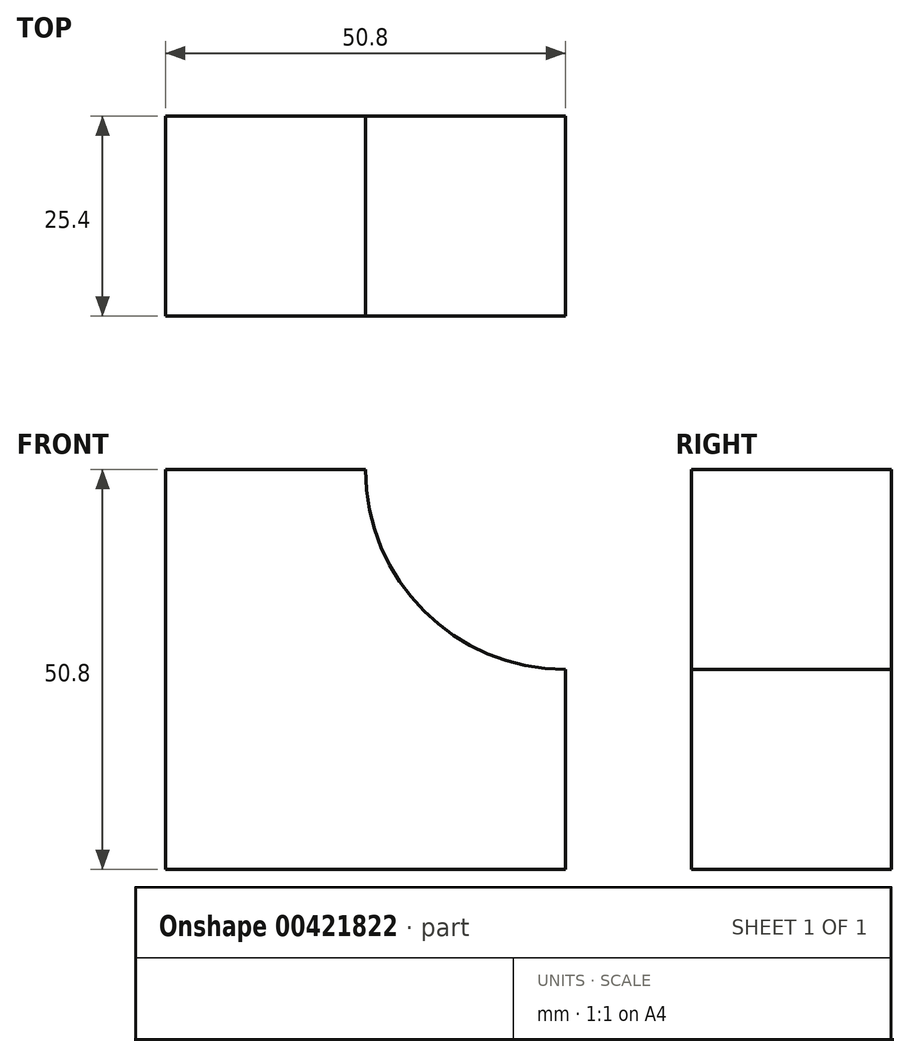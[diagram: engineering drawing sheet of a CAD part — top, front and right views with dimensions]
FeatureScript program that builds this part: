
annotation { "Feature Type Name" : "Feature", "Feature Type Description" : "" }
export const myFeature = defineFeature(function(context is Context, id is Id, definition is map)
    precondition{}
    {
        {
            var Q0;
            Q0=qCreatedBy(makeId("Front.planeOp"),FACE);
            var sketch = newSketch(context, id + "F0", { "sketchPlane" : qUnion([Q0])});
            skLineSegment(sketch, "E0", {"start": v(0, 0) * mm, "end": v(-50.8, 0) * mm});
            skLineSegment(sketch, "E1", {"start": v(-50.8, 0) * mm, "end": v(-50.8, 50.8) * mm});
            skLineSegment(sketch, "E2", {"start": v(-50.8, 50.8) * mm, "end": v(-25.4, 50.8) * mm});
            skArc(sketch, "E3", {"start": v(-25.4, 50.8) * mm, "mid": v(-17.96, 32.84) * mm, "end": v(0, 25.4) * mm});
            skLineSegment(sketch, "E4", {"start": v(0, 0) * mm, "end": v(0, 25.4) * mm});
            skSolve(sketch);
        }
        {
            var Q0;
            Q0 = qSketchRegion(id + "F0", true);
            extrude(context, id + "F1", {"entities" : qUnion([Q0]), "depth" : 25.4 * mm});
        }
    });
